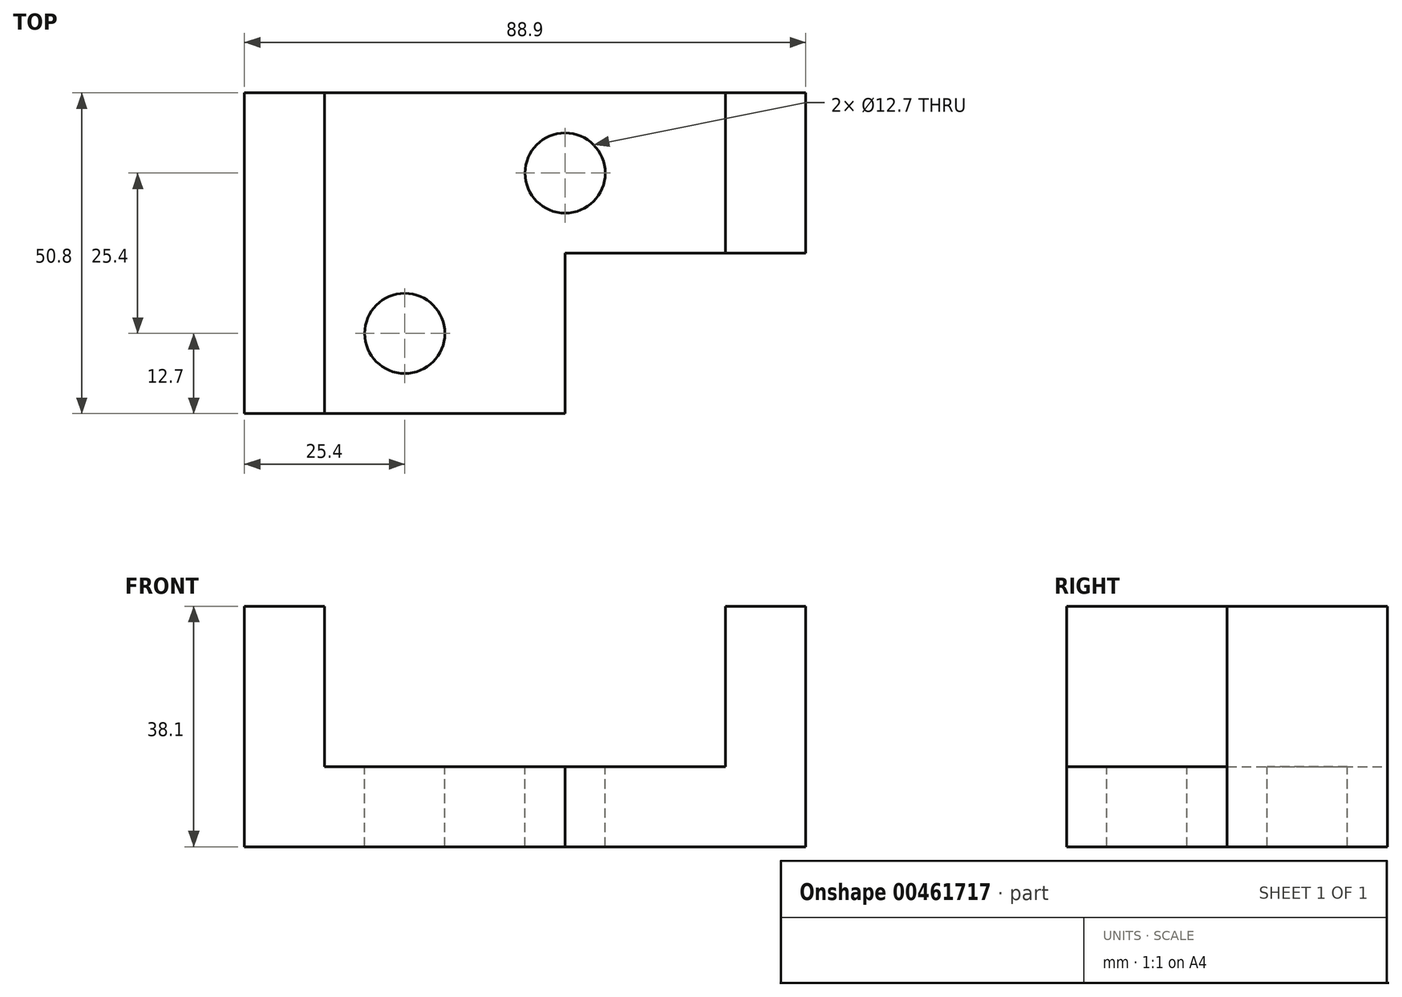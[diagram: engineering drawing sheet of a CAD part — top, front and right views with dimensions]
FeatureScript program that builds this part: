
annotation { "Feature Type Name" : "Feature", "Feature Type Description" : "" }
export const myFeature = defineFeature(function(context is Context, id is Id, definition is map)
    precondition{}
    {
        {
            var Q0;
            Q0=qCreatedBy(makeId("Front.planeOp"),FACE);
            var sketch = newSketch(context, id + "F0", { "sketchPlane" : qUnion([Q0])});
            skLineSegment(sketch, "E0.bottom", {"start": v(-44.45, 19.05) * mm, "end": v(44.45, 19.05) * mm});
            skLineSegment(sketch, "E0.top", {"start": v(-44.45, -19.05) * mm, "end": v(44.45, -19.05) * mm});
            skLineSegment(sketch, "E0.left", {"start": v(-44.45, 19.05) * mm, "end": v(-44.45, -19.05) * mm});
            skLineSegment(sketch, "E0.right", {"start": v(44.45, 19.05) * mm, "end": v(44.45, -19.05) * mm});
            skPoint(sketch, "E0.middle", {"position": v(0, 0) * mm});
            skSolve(sketch);
        }
        {
            var Q0;
            Q0=makeQuery(id+"F0.imprint","IMPRINT",FACE,{"disambiguationData":[TD([[makeQuery(id+"F0.imprint","IMPRINT",EDGE,{"derivedFrom":sQuery(id+"F0.wireOp",EDGE,"E0.bottom")}),-1.0]])]});
            extrude(context, id + "F1", {"entities" : qUnion([Q0]), "depth" : 50.8 * mm});
        }
        {
            var Q0;
            Q0=makeQuery(id+"F1.opExtrude","SWEPT_FACE",FACE,{"disambiguationData":[OSD([sQuery(id+"F0.wireOp",EDGE,"E0.bottom")])]});
            var sketch = newSketch(context, id + "F2", { "sketchPlane" : qUnion([Q0])});
            skLineSegment(sketch, "E1.bottom", {"start": v(6.35, -25.4) * mm, "end": v(44.45, -25.4) * mm});
            skLineSegment(sketch, "E1.top", {"start": v(6.35, -50.8) * mm, "end": v(44.45, -50.8) * mm});
            skLineSegment(sketch, "E1.left", {"start": v(6.35, -25.4) * mm, "end": v(6.35, -50.8) * mm});
            skLineSegment(sketch, "E1.right", {"start": v(44.45, -25.4) * mm, "end": v(44.45, -50.8) * mm});
            skSolve(sketch);
        }
        {
            var Q0;
            Q0=makeQuery(id+"F2.imprint","IMPRINT",FACE,{"disambiguationData":[TD([[makeQuery(id+"F2.imprint","IMPRINT",EDGE,{"derivedFrom":sQuery(id+"F2.wireOp",EDGE,"E1.bottom")}),-1.0]])]});
            extrude(context, id + "F3", {"entities" : qUnion([Q0]), "operationType" : NewBodyOperationType.REMOVE, "oppositeDirection" : true, "depth" : 49.78 * mm});
        }
        {
            var Q0;
            Q0=makeQuery(id+"F1.opExtrude","CAP_FACE",FACE,{"disambiguationData":[OSD([sQuery(id+"F0.wireOp",EDGE,"E0.bottom"),sQuery(id+"F0.wireOp",EDGE,"E0.top"),sQuery(id+"F0.wireOp",EDGE,"E0.left"),sQuery(id+"F0.wireOp",EDGE,"E0.right")])],"isStart":true});
            var sketch = newSketch(context, id + "F4", { "sketchPlane" : qUnion([Q0])});
            skLineSegment(sketch, "E2.bottom", {"start": v(-31.75, 19.05) * mm, "end": v(31.75, 19.05) * mm});
            skLineSegment(sketch, "E2.top", {"start": v(-31.75, -6.35) * mm, "end": v(31.75, -6.35) * mm});
            skLineSegment(sketch, "E2.left", {"start": v(-31.75, 19.05) * mm, "end": v(-31.75, -6.35) * mm});
            skLineSegment(sketch, "E2.right", {"start": v(31.75, 19.05) * mm, "end": v(31.75, -6.35) * mm});
            skSolve(sketch);
        }
        {
            var Q0;
            Q0=makeQuery(id+"F4.imprint","IMPRINT",FACE,{"disambiguationData":[TD([[makeQuery(id+"F4.imprint","IMPRINT",EDGE,{"derivedFrom":sQuery(id+"F4.wireOp",EDGE,"E2.bottom")}),1.0]])]});
            extrude(context, id + "F5", {"entities" : qUnion([Q0]), "operationType" : NewBodyOperationType.REMOVE, "oppositeDirection" : true, "depth" : 71.37 * mm});
        }
        {
            var Q0;
            Q0=makeQuery(id+"F5.boolean.opBoolean","COPY",FACE,{"derivedFrom":makeQuery(id+"F5.opExtrude","SWEPT_FACE",FACE,{"disambiguationData":[OSD([sQuery(id+"F4.wireOp",EDGE,"E2.top")])]})});
            var sketch = newSketch(context, id + "F6", { "sketchPlane" : qUnion([Q0])});
            skCircle(sketch, "E3", {"center": v(-19.05, -38.1) * mm, "radius": 6.35 * mm});
            skCircle(sketch, "E4", {"center": v(6.35, -12.7) * mm, "radius": 6.35 * mm});
            skSolve(sketch);
        }
        {
            var Q0;
            Q0 = qSketchRegion(id + "F6", true);
            extrude(context, id + "F7", {"entities" : qUnion([Q0]), "operationType" : NewBodyOperationType.REMOVE, "oppositeDirection" : true, "depth" : 25.4 * mm});
        }
    });
